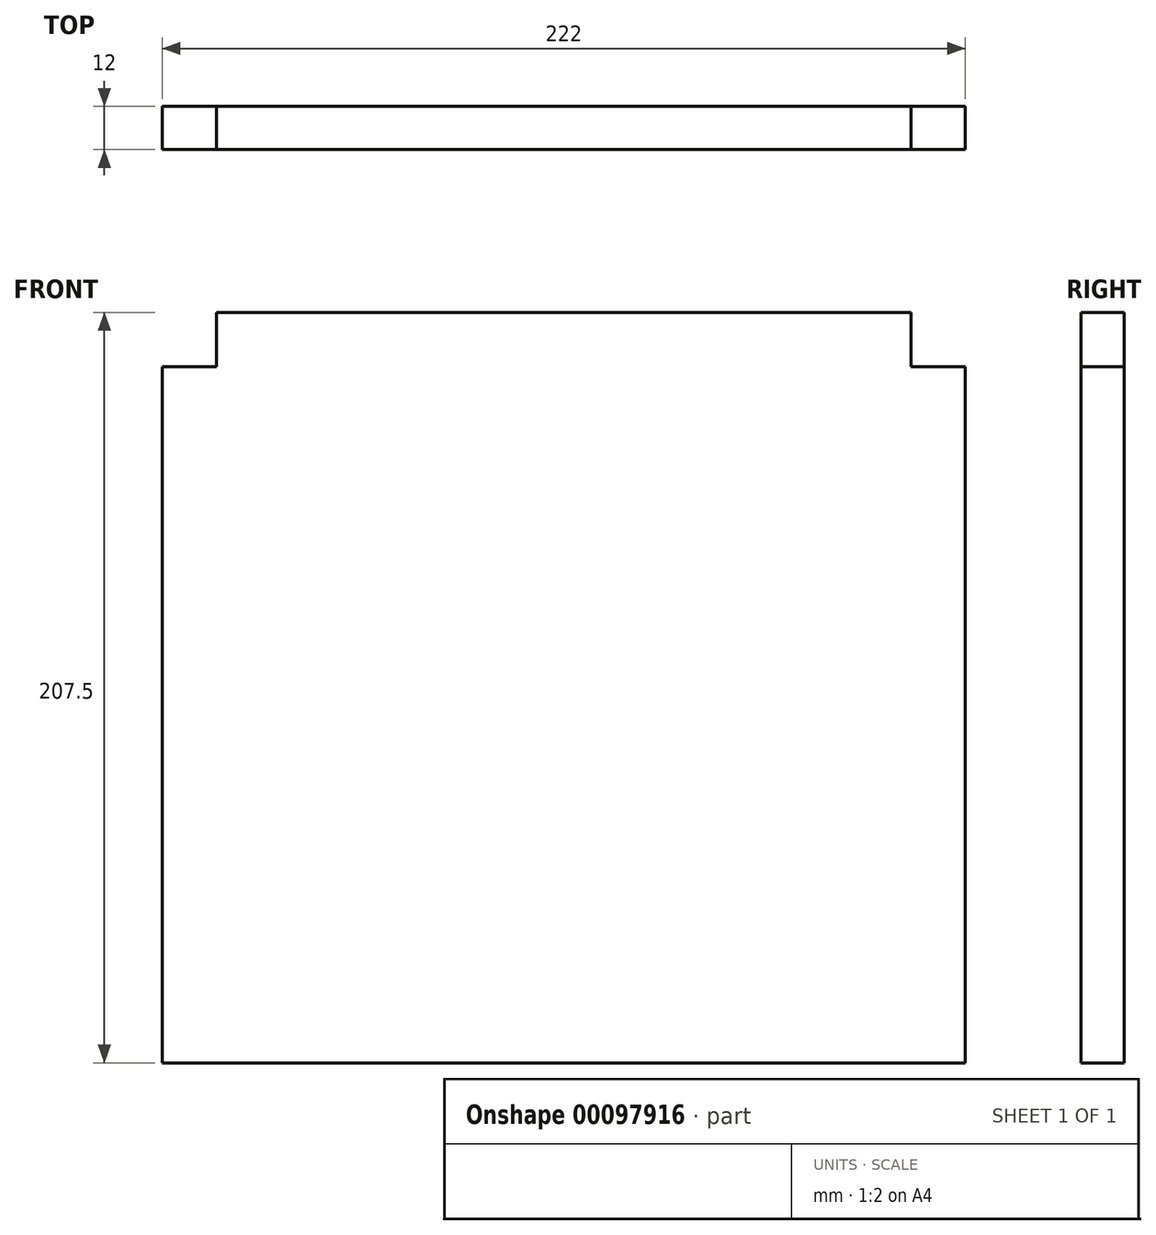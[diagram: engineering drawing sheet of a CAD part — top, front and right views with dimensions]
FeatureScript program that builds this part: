
annotation { "Feature Type Name" : "Feature", "Feature Type Description" : "" }
export const myFeature = defineFeature(function(context is Context, id is Id, definition is map)
    precondition{}
    {
        {
            var Q0;
            Q0=qCreatedBy(makeId("Front.planeOp"),FACE);
            var sketch = newSketch(context, id + "F0", { "sketchPlane" : qUnion([Q0])});
            skLineSegment(sketch, "E0.bottom", {"start": v(-222, 207.5) * mm, "end": v(0, 207.5) * mm});
            skLineSegment(sketch, "E0.top", {"start": v(-222, 0) * mm, "end": v(0, 0) * mm});
            skLineSegment(sketch, "E0.left", {"start": v(-222, 207.5) * mm, "end": v(-222, 0) * mm});
            skLineSegment(sketch, "E0.right", {"start": v(0, 207.5) * mm, "end": v(0, 0) * mm});
            skSolve(sketch);
        }
        {
            var Q0;
            Q0=makeQuery(id+"F0.imprint","IMPRINT",FACE,{"disambiguationData":[TD([[makeQuery(id+"F0.imprint","IMPRINT",EDGE,{"derivedFrom":sQuery(id+"F0.wireOp",EDGE,"E0.bottom")}),-1.0]])]});
            extrude(context, id + "F1", {"entities" : qUnion([Q0]), "depth" : 12 * mm});
        }
        {
            var Q0;
            Q0=makeQuery(id+"F1.opExtrude","CAP_FACE",FACE,{"disambiguationData":[OSD([sQuery(id+"F0.wireOp",EDGE,"E0.bottom"),sQuery(id+"F0.wireOp",EDGE,"E0.top"),sQuery(id+"F0.wireOp",EDGE,"E0.left"),sQuery(id+"F0.wireOp",EDGE,"E0.right")])],"isStart":false});
            var sketch = newSketch(context, id + "F2", { "sketchPlane" : qUnion([Q0])});
            skLineSegment(sketch, "E1.bottom", {"start": v(0, 207.5) * mm, "end": v(-15, 207.5) * mm});
            skLineSegment(sketch, "E1.top", {"start": v(0, 192.5) * mm, "end": v(-15, 192.5) * mm});
            skLineSegment(sketch, "E1.left", {"start": v(0, 207.5) * mm, "end": v(0, 192.5) * mm});
            skLineSegment(sketch, "E1.right", {"start": v(-15, 207.5) * mm, "end": v(-15, 192.5) * mm});
            skLineSegment(sketch, "E2.bottom", {"start": v(-222, 207.5) * mm, "end": v(-207, 207.5) * mm});
            skLineSegment(sketch, "E2.top", {"start": v(-222, 192.5) * mm, "end": v(-207, 192.5) * mm});
            skLineSegment(sketch, "E2.left", {"start": v(-222, 207.5) * mm, "end": v(-222, 192.5) * mm});
            skLineSegment(sketch, "E2.right", {"start": v(-207, 207.5) * mm, "end": v(-207, 192.5) * mm});
            skSolve(sketch);
        }
        {
            var Q0;
            Q0=makeQuery(id+"F2.imprint","IMPRINT",FACE,{"disambiguationData":[TD([[makeQuery(id+"F2.imprint","IMPRINT",EDGE,{"derivedFrom":sQuery(id+"F2.wireOp",EDGE,"E1.bottom")}),-1.0]])]});
            var Q1;
            Q1=makeQuery(id+"F2.imprint","IMPRINT",FACE,{"disambiguationData":[TD([[makeQuery(id+"F2.imprint","IMPRINT",EDGE,{"derivedFrom":sQuery(id+"F2.wireOp",EDGE,"E2.bottom")}),-1.0]])]});
            extrude(context, id + "F3", {"entities" : qUnion([Q0, Q1]), "operationType" : NewBodyOperationType.REMOVE, "oppositeDirection" : true, "depth" : 25 * mm});
        }
    });
